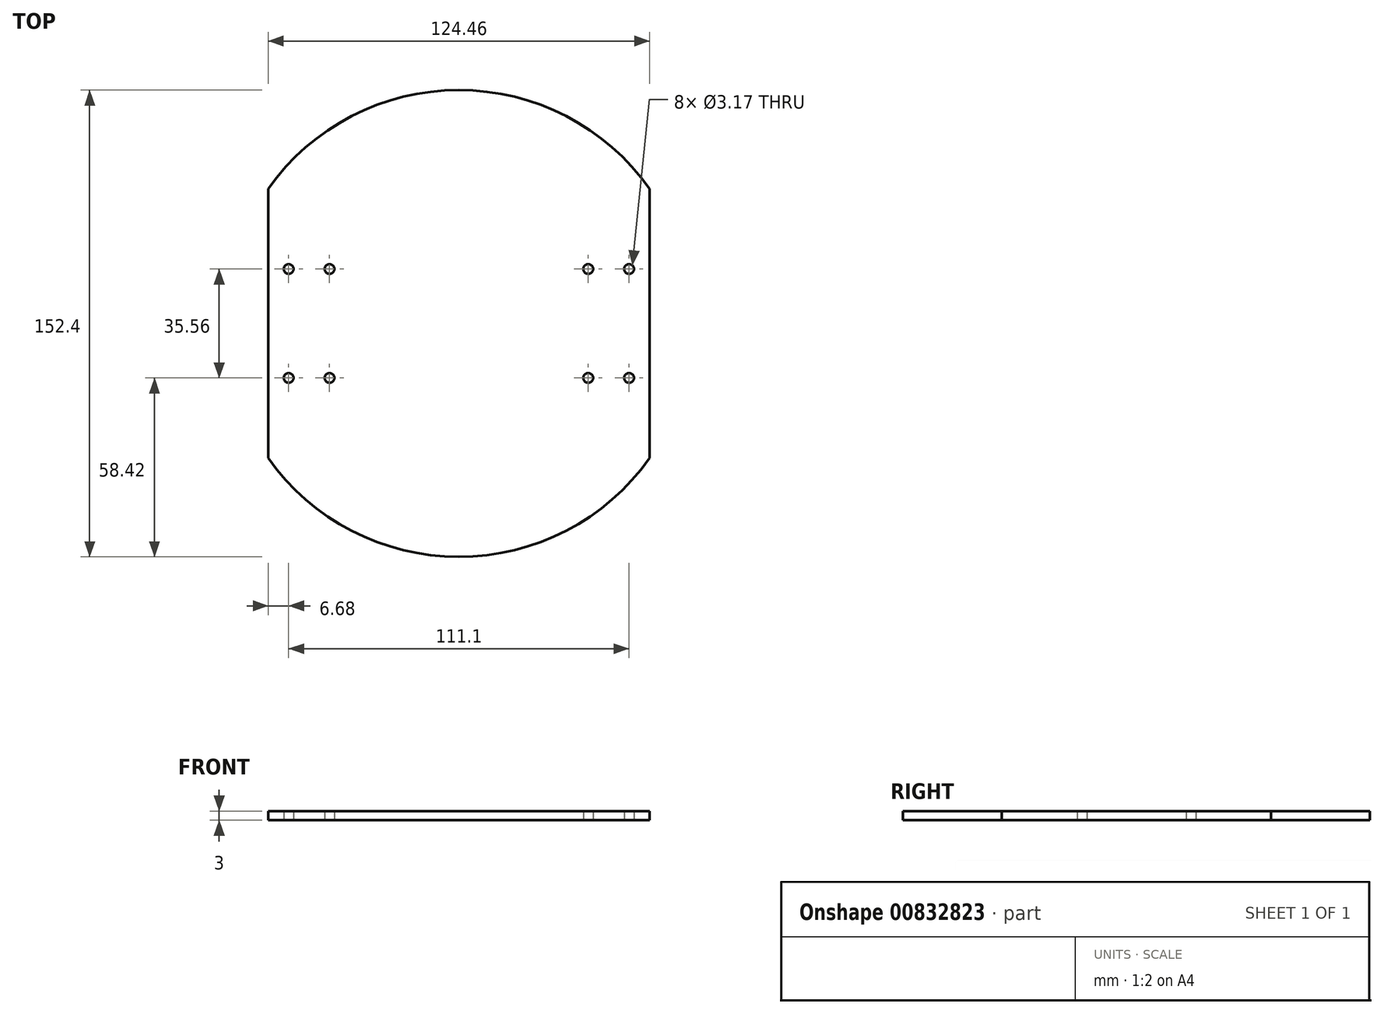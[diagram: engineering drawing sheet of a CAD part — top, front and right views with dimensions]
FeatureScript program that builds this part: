
annotation { "Feature Type Name" : "Feature", "Feature Type Description" : "" }
export const myFeature = defineFeature(function(context is Context, id is Id, definition is map)
    precondition{}
    {
        {
            var Q0;
            Q0=qCreatedBy(makeId("Top.planeOp"),FACE);
            var sketch = newSketch(context, id + "F0", { "sketchPlane" : qUnion([Q0])});
            skArc(sketch, "E0", {"start": v(-62.23, -43.98) * mm, "mid": v(0, -76.2) * mm, "end": v(62.23, -43.98) * mm});
            skLineSegment(sketch, "E1", {"start": v(-62.23, 43.98) * mm, "end": v(-62.23, -43.98) * mm});
            skLineSegment(sketch, "E2.MirrorCS", {"start": v(62.23, 43.98) * mm, "end": v(62.23, -43.98) * mm});
            skArc(sketch, "E3.trimOffspring", {"start": v(62.23, 43.98) * mm, "mid": v(0, 76.2) * mm, "end": v(-62.23, 43.98) * mm});
            skCircle(sketch, "E4", {"center": v(-55.55, 17.78) * mm, "radius": 1.59 * mm});
            skCircle(sketch, "E5", {"center": v(-42.21, 17.78) * mm, "radius": 1.59 * mm});
            skCircle(sketch, "E6", {"center": v(-55.55, -17.78) * mm, "radius": 1.59 * mm});
            skCircle(sketch, "E7", {"center": v(-42.21, -17.78) * mm, "radius": 1.59 * mm});
            skCircle(sketch, "E8.MirrorC", {"center": v(42.21, -17.78) * mm, "radius": 1.59 * mm});
            skCircle(sketch, "E9.MirrorC", {"center": v(55.55, -17.78) * mm, "radius": 1.59 * mm});
            skCircle(sketch, "E10.MirrorC", {"center": v(42.21, 17.78) * mm, "radius": 1.59 * mm});
            skCircle(sketch, "E11.MirrorC", {"center": v(55.55, 17.78) * mm, "radius": 1.59 * mm});
            skSolve(sketch);
        }
        {
            var Q0;
            Q0 = qSketchRegion(id + "F0", true);
            extrude(context, id + "F1", {"entities" : qUnion([Q0]), "depth" : 3 * mm, "offsetDistance" : 25.4 * mm});
        }
    });
